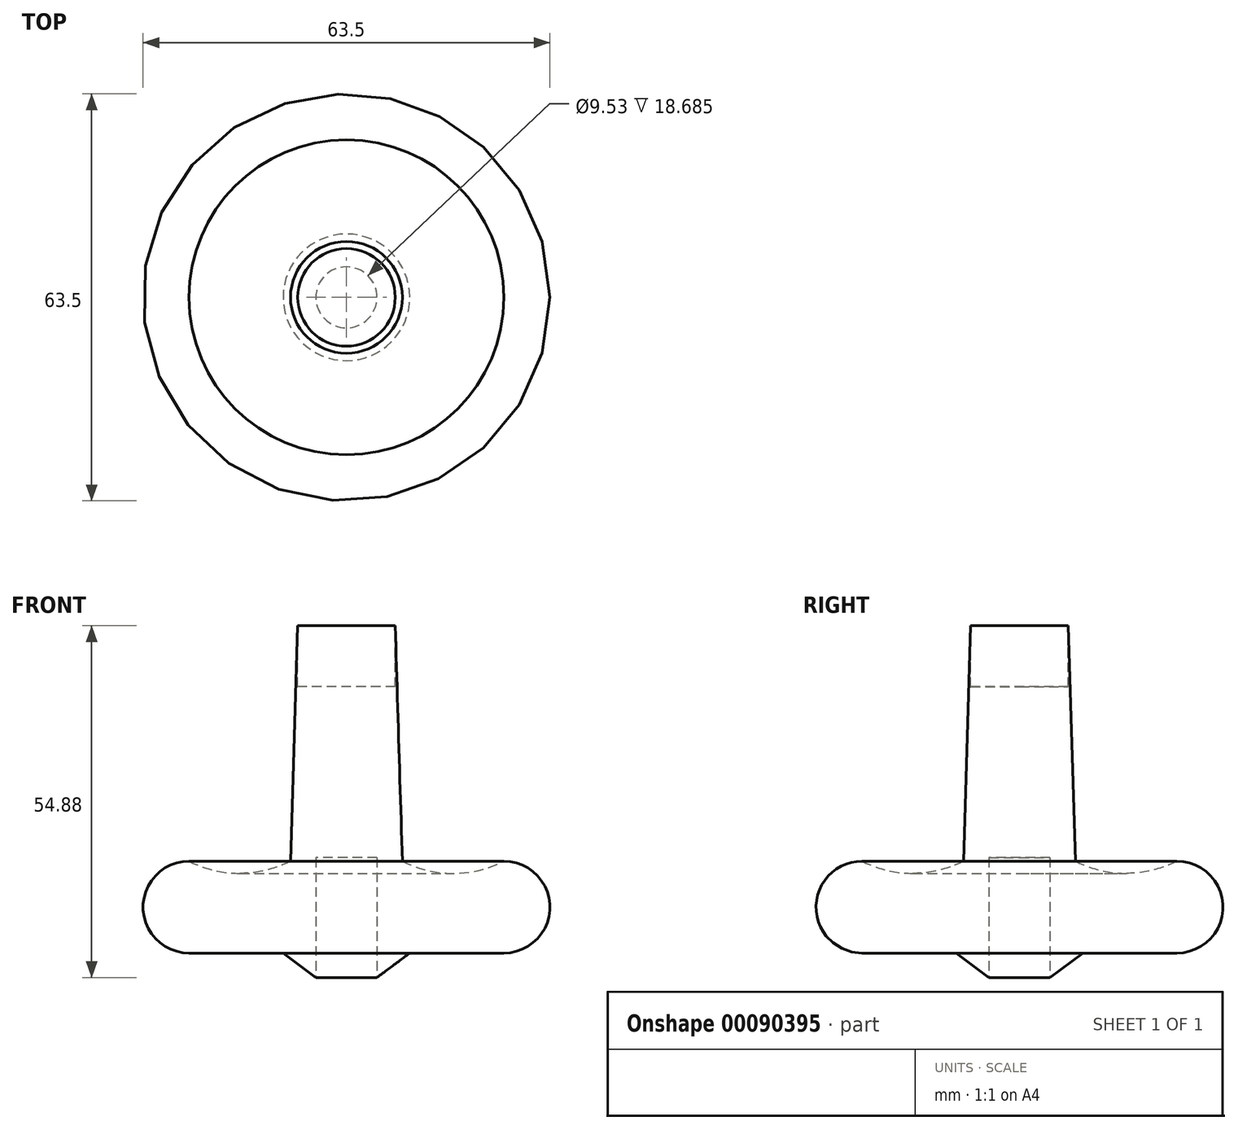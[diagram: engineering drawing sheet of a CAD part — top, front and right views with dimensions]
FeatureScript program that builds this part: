
annotation { "Feature Type Name" : "Feature", "Feature Type Description" : "" }
export const myFeature = defineFeature(function(context is Context, id is Id, definition is map)
    precondition{}
    {
        {
            var Q0;
            Q0=qCreatedBy(makeId("Front.planeOp"),FACE);
            var sketch = newSketch(context, id + "F0", { "sketchPlane" : qUnion([Q0])});
            skLineSegment(sketch, "E0", {"start": v(0, 0) * mm, "end": v(9.88, 7.35) * mm});
            skLineSegment(sketch, "E1", {"start": v(9.88, 7.35) * mm, "end": v(24.58, 7.35) * mm});
            skArc(sketch, "E2", {"start": v(24.58, 7.35) * mm, "mid": v(31.75, 14.52) * mm, "end": v(24.58, 21.7) * mm});
            skArc(sketch, "E3", {"start": v(8.72, 21.7) * mm, "mid": v(16.65, 19.8) * mm, "end": v(24.58, 21.7) * mm});
            skLineSegment(sketch, "E4", {"start": v(8.72, 21.7) * mm, "end": v(7.62, 58.42) * mm});
            skLineSegment(sketch, "E5", {"start": v(7.62, 58.42) * mm, "end": v(0, 58.42) * mm});
            skLineSegment(sketch, "E6", {"start": v(0, 58.42) * mm, "end": v(0, 0) * mm});
            skPoint(sketch, "E7", {"position": v(31.75, 14.52) * mm});
            skSolve(sketch);
        }
        {
            var Q0;
            Q0=makeQuery(id+"F0.imprint","IMPRINT",FACE,{"disambiguationData":[TD([[makeQuery(id+"F0.imprint","IMPRINT",EDGE,{"derivedFrom":sQuery(id+"F0.wireOp",EDGE,"E0")}),1.0]])]});
            var Q1;
            Q1 = qSketchRegion(id + "F2", true);
            var Q2;
            Q2=sQuery(id+"F0.wireOp",EDGE,"E6");
            revolve(context, id + "F1", {"entities" : qUnion([Q0, Q1]), "axis" : qUnion([Q2]), "revolveType" : RevolveType.FULL});
        }
        {
            var Q0;
            Q0=qCreatedBy(makeId("Top.planeOp"),FACE);
            var sketch = newSketch(context, id + "F2", { "sketchPlane" : qUnion([Q0])});
            skCircle(sketch, "E8", {"center": v(0, 0) * mm, "radius": 4.76 * mm});
            skSolve(sketch);
        }
        {
            var Q0;
            Q0 = qSketchRegion(id + "F2", true);
            var Q1;
            Q1=makeQuery(id+"F1.opRevolve","SWEPT_FACE",FACE,{"disambiguationData":[OSD([sQuery(id+"F0.wireOp",EDGE,"E5")])]});
            extrude(context, id + "F3", {"entities" : qUnion([Q0, Q1]), "operationType" : NewBodyOperationType.REMOVE, "oppositeDirection" : true, "depth" : 9.52 * mm});
        }
        {
            var Q0;
            Q0 = qSketchRegion(id + "F2", true);
            extrude(context, id + "F4", {"entities" : qUnion([Q0]), "operationType" : NewBodyOperationType.REMOVE, "depth" : 22.22 * mm});
        }
    });
